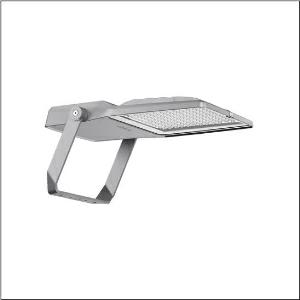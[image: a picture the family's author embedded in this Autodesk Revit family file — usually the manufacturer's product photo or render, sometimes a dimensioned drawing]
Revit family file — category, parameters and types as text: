
# Revit family: floodlight_fl_21_iq_midi___rs12_5xa7782f5b1a_9a70
name_source: partatom
category: Lighting Fixtures
units: mm (PartAtom-declared; Revit-internal decimal feet)

## family parameters
Cut with Voids When Loaded = No
Host = Face
Light Source = No
Part Type = Normal
Room Calculation Point = No
Round Connector Dimension = Use Diameter
Shared = No

## types (1)
- --- (1 x LED, 33220 lm, 270.2 W, 4000K)
    Apparent Load = 270 VA
    CIE Flux Codes = 79 92 99 100 100
    Color Rendering = 80
    Color Temperature = 4000K
    Default Elevation = 1800 mm
    Description = Floodlight FL 21 iQ midi, floodlight, primary light control with lens, of PMMA, primary optical cover: protective disc, of toughened safety glass, transparent, light distribution: RS12, light emission: direct distribution, installation type: surface-mounted, LED, High Power LED, rated luminous flux: 33.220lm, luminous efficacy: 123lm/W, light colour: 840, colour temperature: 4000K, control gear: ECG iQ, control: optimised constant luminous flux control (CLO 2.0), Desk-Remote (wireless, voltage-free reading and setting of iQ features in the workshop via application-optimized NFC function/RFID function), Smart-Wire, Night-Set, Temp-Guard, Street-Remote, Auto-Match, with terminal, 6-pole, mains connection: 220..240V, AC, 50/60Hz, start of lifetime: 270W, end of service life: 287W, reduction: 118W, luminaire housing, of diecast aluminium, powder-coated, Siteco® metallic grey (DB 702S), corrosivity category C5 mid according to DIN EN ISO 12944, sealing non-destructively replaceable, mounting bracket, of steel, galvanised, powder-coated, Siteco® metallic grey (DB 702S), protection rating (complete): IP66, insulation class (complete): insulation class II (safety insulation), certification: CE, protection symbol: D, impact resistance: IK08, permissible operating ambient temperature: -40..+40°C, permissible operating ambient temperature for outdoor applications: -40..+50°C, standard: DIN EN 12944, LABS conformity tested according to VDMA 24364:2018-05, packaging unit: 1 piece

Light Distribution: RS12
    Height = 76 mm
    Lamp = 1 x LED
    Lamp Light Flux = 33220 lm
    Lamp Power = 270.2 W
    Lamp count = 1
    Length = 657 mm
    Luminous efficacy = 123 lm/W
    Manufacturer = Siteco
    ModVariant = No
    Model = 5XA7782F5B1A
    Number of Poles = 1
    OnlyDefault = Yes
    Power Factor = 1
    Product Name = Floodlight FL 21 iQ midi | RS12
    Product group = floodlight | pylon annexe
    ProductGroupID = 6200
    Protection Class = Protection class II
    Protection Degree = IP 66
    RLX_Detail_Level = 1
    RLX_Emergency_Light_Flux = 0 lm
    RLX_Emergency_Type = 0
    RLX_Emergency_Type_DB = No
    RlxData = <blob elided: 141273 chars, md5=b5b2d01b>
    Socket = socket
    Standby Power = 0 W
    System Light Flux = 33220 lm
    System Power = 270 W
    Type Comments = factory setting: luminous flux: 100 % | dim-lin: 254 | 620 mA
    Type Image = l_1006876.jpg
    URL = http://relux.com
    VarID = @adj_055685
    Voltage = 0 V
    Weight = 0.00 kg
    Width = 442 mm

## geometry (parser evidence)
native form markers: Blend x4, Sweep x13
no freeform markers — native parametric forms only
